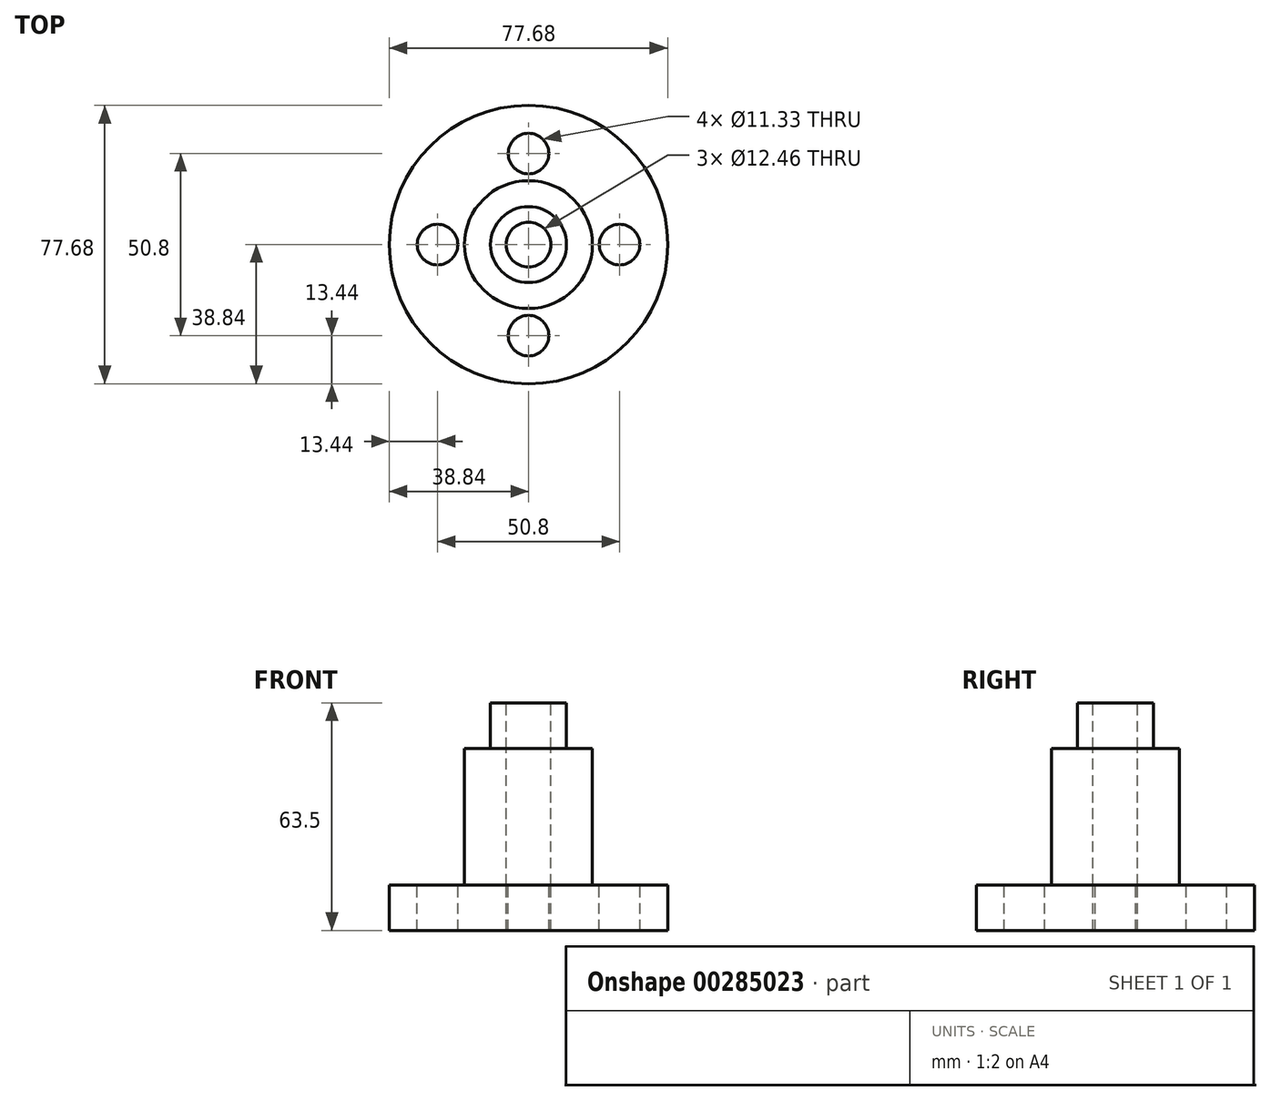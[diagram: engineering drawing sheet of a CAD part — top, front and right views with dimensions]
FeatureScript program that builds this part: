
annotation { "Feature Type Name" : "Feature", "Feature Type Description" : "" }
export const myFeature = defineFeature(function(context is Context, id is Id, definition is map)
    precondition{}
    {
        {
            var Q0;
            Q0=qCreatedBy(makeId("Top.planeOp"),FACE);
            var sketch = newSketch(context, id + "F0", { "sketchPlane" : qUnion([Q0])});
            skCircle(sketch, "E0", {"center": v(0, 0) * mm, "radius": 38.84 * mm});
            skSolve(sketch);
        }
        {
            var Q0;
            Q0=makeQuery(id+"F0.imprint","IMPRINT",FACE,{"disambiguationData":[TD([[makeQuery(id+"F0.imprint","IMPRINT",EDGE,{"derivedFrom":sQuery(id+"F0.wireOp",EDGE,"E0")}),1.0]])]});
            extrude(context, id + "F1", {"entities" : qUnion([Q0]), "depth" : 12.7 * mm});
        }
        {
            var Q0;
            Q0=makeQuery(id+"F1.opExtrude","CAP_FACE",FACE,{"disambiguationData":[OSD([sQuery(id+"F0.wireOp",EDGE,"E0")])],"isStart":false});
            var sketch = newSketch(context, id + "F2", { "sketchPlane" : qUnion([Q0])});
            skCircle(sketch, "E1", {"center": v(0, 0) * mm, "radius": 17.84 * mm});
            skSolve(sketch);
        }
        {
            var Q0;
            Q0=makeQuery(id+"F2.imprint","IMPRINT",FACE,{"disambiguationData":[TD([[makeQuery(id+"F2.imprint","IMPRINT",EDGE,{"derivedFrom":sQuery(id+"F2.wireOp",EDGE,"E1")}),1.0]])]});
            var Q1;
            Q1=sQuery(id+"F2.wireOp",EDGE,"E1");
            extrude(context, id + "F3", {"entities" : qUnion([Q0]), "surfaceEntities" : qUnion([Q1]), "depth" : 38.1 * mm});
        }
        {
            var Q0;
            Q0=makeQuery(id+"F3.opExtrude","CAP_FACE",FACE,{"disambiguationData":[OSD([sQuery(id+"F2.wireOp",EDGE,"E1")])],"isStart":false});
            var sketch = newSketch(context, id + "F4", { "sketchPlane" : qUnion([Q0])});
            skCircle(sketch, "E2", {"center": v(0, 0) * mm, "radius": 10.6 * mm});
            skSolve(sketch);
        }
        {
            var Q0;
            Q0=makeQuery(id+"F4.imprint","IMPRINT",FACE,{"disambiguationData":[TD([[makeQuery(id+"F4.imprint","IMPRINT",EDGE,{"derivedFrom":sQuery(id+"F4.wireOp",EDGE,"E2")}),1.0]])]});
            var Q1;
            Q1=sQuery(id+"F4.wireOp",EDGE,"E2");
            extrude(context, id + "F5", {"entities" : qUnion([Q0]), "surfaceEntities" : qUnion([Q1]), "depth" : 12.7 * mm});
        }
        {
            var Q0;
            Q0=makeQuery(id+"F5.opExtrude","CAP_FACE",FACE,{"disambiguationData":[OSD([sQuery(id+"F4.wireOp",EDGE,"E2")])],"isStart":false});
            var sketch = newSketch(context, id + "F6", { "sketchPlane" : qUnion([Q0])});
            skCircle(sketch, "E3", {"center": v(0, 0) * mm, "radius": 6.23 * mm});
            skSolve(sketch);
        }
        {
            var Q0;
            Q0=makeQuery(id+"F6.imprint","IMPRINT",FACE,{"disambiguationData":[TD([[makeQuery(id+"F6.imprint","IMPRINT",EDGE,{"derivedFrom":sQuery(id+"F6.wireOp",EDGE,"E3")}),1.0]])]});
            var Q1;
            Q1=sQuery(id+"F6.wireOp",EDGE,"E3");
            extrude(context, id + "F7", {"entities" : qUnion([Q0]), "operationType" : NewBodyOperationType.REMOVE, "surfaceEntities" : qUnion([Q1]), "oppositeDirection" : true, "depth" : 63.5 * mm});
        }
        {
            var Q0;
            Q0=makeQuery(id+"F1.opExtrude","CAP_FACE",FACE,{"disambiguationData":[OSD([sQuery(id+"F0.wireOp",EDGE,"E0")])],"isStart":false});
            var sketch = newSketch(context, id + "F8", { "sketchPlane" : qUnion([Q0])});
            skLineSegment(sketch, "E4", {"start": v(0, 0) * mm, "end": v(0, 25.4) * mm});
            skLineSegment(sketch, "E5", {"start": v(0, 0) * mm, "end": v(0, -25.4) * mm});
            skLineSegment(sketch, "E6", {"start": v(0, 0) * mm, "end": v(25.4, 0) * mm});
            skLineSegment(sketch, "E7", {"start": v(0, 0) * mm, "end": v(-25.4, 0) * mm});
            skCircle(sketch, "E8", {"center": v(0, 25.4) * mm, "radius": 5.66 * mm});
            skCircle(sketch, "E9", {"center": v(25.4, 0) * mm, "radius": 5.66 * mm});
            skCircle(sketch, "E10", {"center": v(0, -25.4) * mm, "radius": 5.66 * mm});
            skCircle(sketch, "E11", {"center": v(-25.4, 0) * mm, "radius": 5.66 * mm});
            skSolve(sketch);
        }
        {
            var Q0;
            Q0 = qSketchRegion(id + "F8", true);
            extrude(context, id + "F9", {"entities" : qUnion([Q0]), "operationType" : NewBodyOperationType.REMOVE, "oppositeDirection" : true, "depth" : 25.4 * mm});
        }
    });
